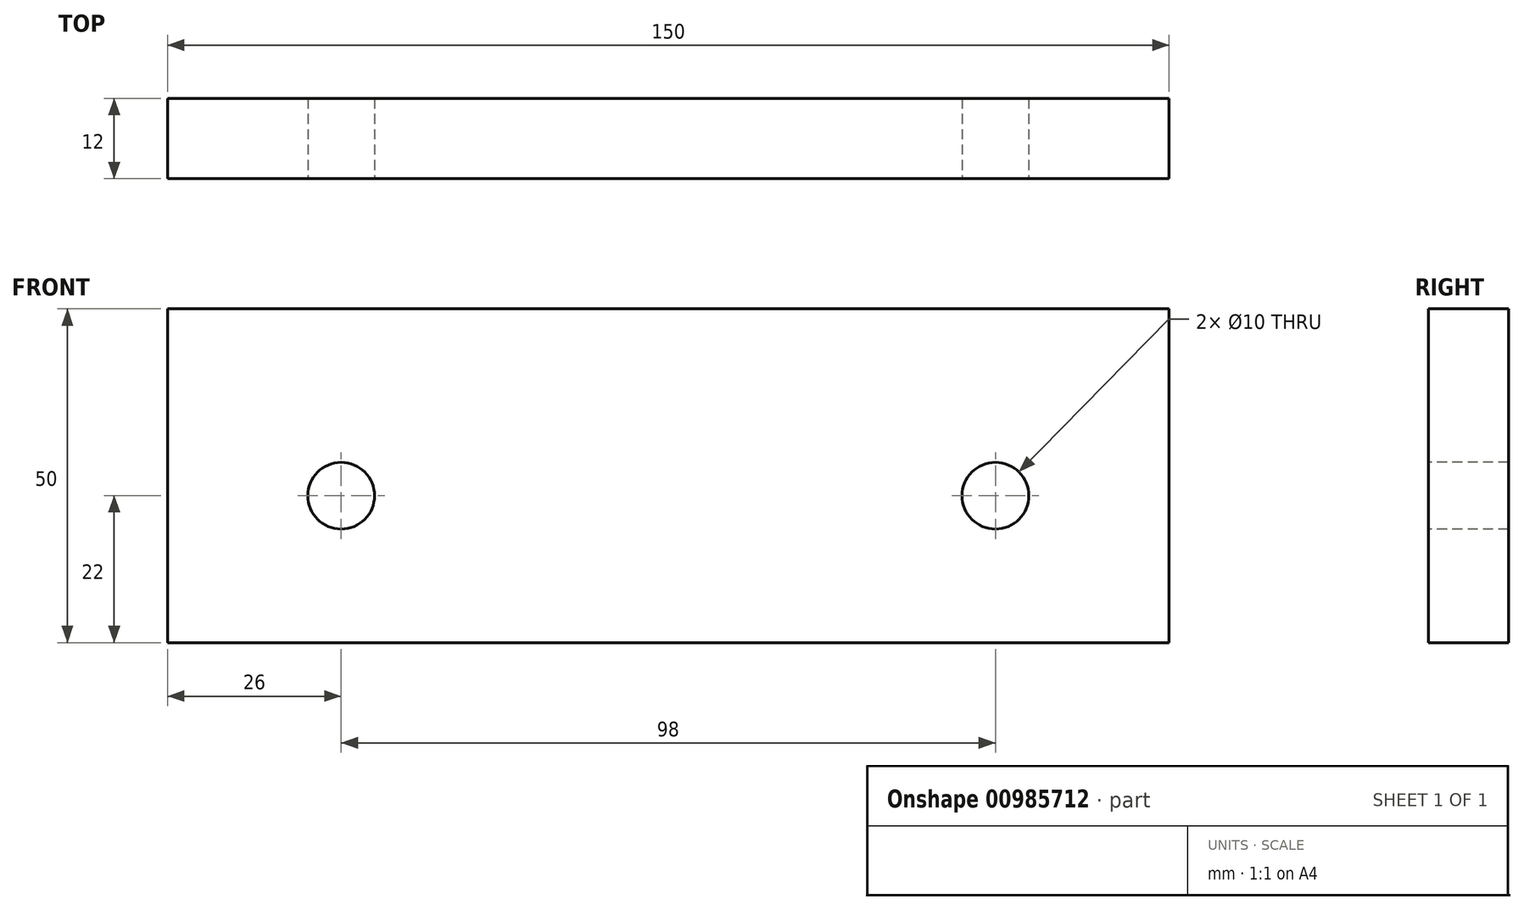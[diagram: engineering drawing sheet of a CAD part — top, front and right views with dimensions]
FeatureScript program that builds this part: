
annotation { "Feature Type Name" : "Feature", "Feature Type Description" : "" }
export const myFeature = defineFeature(function(context is Context, id is Id, definition is map)
    precondition{}
    {
        {
            var Q0;
            Q0=qCreatedBy(makeId("Front.planeOp"),FACE);
            var sketch = newSketch(context, id + "F0", { "sketchPlane" : qUnion([Q0])});
            skLineSegment(sketch, "E0.bottom", {"start": v(75, 25) * mm, "end": v(-75, 25) * mm});
            skLineSegment(sketch, "E0.top", {"start": v(75, -25) * mm, "end": v(-75, -25) * mm});
            skLineSegment(sketch, "E0.left", {"start": v(75, 25) * mm, "end": v(75, -25) * mm});
            skLineSegment(sketch, "E0.right", {"start": v(-75, 25) * mm, "end": v(-75, -25) * mm});
            skPoint(sketch, "E0.middle", {"position": v(0, 0) * mm});
            skLineSegment(sketch, "E1", {"start": v(0, 25) * mm, "end": v(0, -25) * mm, "construction": true});
            skPoint(sketch, "E2", {"position": v(-49, -3) * mm});
            skPoint(sketch, "E3", {"position": v(49, -3) * mm});
            skSolve(sketch);
        }
        {
            var Q0;
            Q0 = qSketchRegion(id + "F0", true);
            extrude(context, id + "F1", {"entities" : qUnion([Q0]), "oppositeDirection" : true, "depth" : 12 * mm, "offsetDistance" : 25 * mm});
        }
        {
            var Q0;
            Q0=sQuery(id+"F0.wireOp",VERTEX,"E2");
            var Q1;
            Q1=sQuery(id+"F0.wireOp",VERTEX,"E3");
            var Q2;
            Q2=makeQuery(id+"F1.opExtrude","SWEPT_BODY",BODY,{"disambiguationData":[OSD([sQuery(id+"F0.wireOp",EDGE,"E0.bottom"),sQuery(id+"F0.wireOp",EDGE,"E0.top"),sQuery(id+"F0.wireOp",EDGE,"E0.left"),sQuery(id+"F0.wireOp",EDGE,"E0.right")])]});
            hole(context, id + "F2", {"style" : HoleStyle.SIMPLE, "endStyle" : HoleEndStyle.THROUGH, "standardTappedOrClearance" : lookupTablePath({ "standard" : "ISO", "size" : "10", "type" : "Drilled" }), "standardBlindInLast" : lookupTablePath({ "standard" : "ISO", "size" : "10", "type" : "Drilled" }), "holeDiameter" : 10 * mm, "majorDiameter" : 2.2 * mm, "tappedDepth" : 4.25 * mm, "tapClearance" : 3, "locations" : qUnion([Q0, Q1]), "scope" : qUnion([Q2])});
        }
    });
